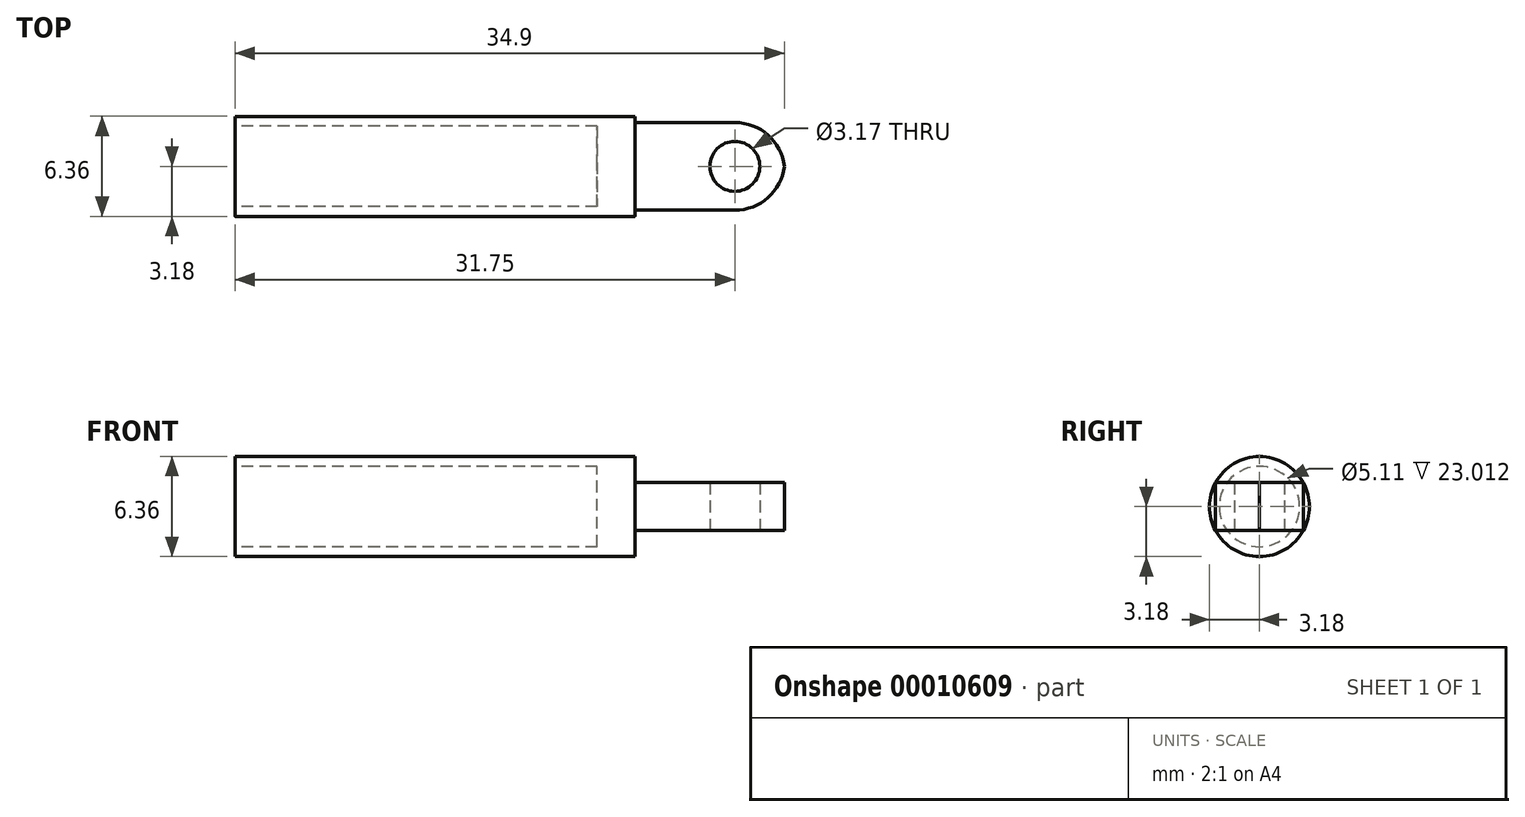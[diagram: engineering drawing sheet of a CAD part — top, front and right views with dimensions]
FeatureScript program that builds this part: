
annotation { "Feature Type Name" : "Feature", "Feature Type Description" : "" }
export const myFeature = defineFeature(function(context is Context, id is Id, definition is map)
    precondition{}
    {
        {
            var Q0;
            Q0=qCreatedBy(makeId("Right.planeOp"),FACE);
            var sketch = newSketch(context, id + "F0", { "sketchPlane" : qUnion([Q0])});
            skCircle(sketch, "E0", {"center": v(0, 0) * mm, "radius": 3.17 * mm});
            skCircle(sketch, "E1", {"center": v(0, 0) * mm, "radius": 2.55 * mm});
            skSolve(sketch);
        }
        {
            var Q0;
            Q0=qSketchRegion(id+"F0",true);
            var Q1;
            Q1=makeQuery(id+"F0.imprint","IMPRINT",FACE,{"disambiguationData":[TD([[makeQuery(id+"F0.imprint","IMPRINT",EDGE,{"derivedFrom":sQuery(id+"F0.wireOp",EDGE,"E1")}),1.0]])]});
            extrude(context, id + "F1", {"entities" : qUnion([Q0, Q1]), "depth" : 25.4 * mm});
        }
        {
            var Q0;
            Q0=makeQuery(id+"F0.imprint","IMPRINT",FACE,{"disambiguationData":[TD([[makeQuery(id+"F0.imprint","IMPRINT",EDGE,{"derivedFrom":sQuery(id+"F0.wireOp",EDGE,"E1")}),1.0]])]});
            extrude(context, id + "F2", {"entities" : qUnion([Q0]), "operationType" : NewBodyOperationType.REMOVE, "depth" : 23.01 * mm});
        }
        {
            var Q0;
            Q0=makeQuery(id+"F1.opExtrude","CAP_FACE",FACE,{"disambiguationData":[OSD([sQuery(id+"F0.wireOp",EDGE,"E0")])],"isStart":false});
            var sketch = newSketch(context, id + "F3", { "sketchPlane" : qUnion([Q0])});
            skCircle(sketch, "E2.0", {"center": v(0, 0) * mm, "radius": 3.17 * mm, "construction": true});
            skLineSegment(sketch, "E3.rect.bottom", {"start": v(-2.79, -1.52) * mm, "end": v(2.79, -1.52) * mm});
            skLineSegment(sketch, "E3.rect.top", {"start": v(-2.79, 1.52) * mm, "end": v(2.79, 1.52) * mm});
            skLineSegment(sketch, "E3.rect.left", {"start": v(-2.79, -1.52) * mm, "end": v(-2.79, 1.52) * mm});
            skLineSegment(sketch, "E3.rect.right", {"start": v(2.79, -1.52) * mm, "end": v(2.79, 1.52) * mm});
            skSolve(sketch);
        }
        {
            var Q0;
            Q0=qSketchRegion(id+"F3",true);
            extrude(context, id + "F4", {"entities" : qUnion([Q0]), "operationType" : NewBodyOperationType.ADD, "depth" : 9.52 * mm});
        }
        {
            var Q0;
            Q0=makeQuery(id+"F4.opExtrude","CAP_EDGE",EDGE,{"disambiguationData":[OSD([sQuery(id+"F3.wireOp",EDGE,"E3.rect.left")])],"isStart":false});
            var Q1;
            Q1=makeQuery(id+"F4.opExtrude","CAP_EDGE",EDGE,{"disambiguationData":[OSD([sQuery(id+"F3.wireOp",EDGE,"E3.rect.right")])],"isStart":false});
            fillet(context, id + "F5", {"entities" : qUnion([Q0, Q1]), "radius" : 3.17 * mm, "tangentPropagation" : true, "allowEdgeOverflow" : false});
        }
        {
            var Q0;
            Q0=makeQuery(id+"F4.opExtrude","SWEPT_FACE",FACE,{"disambiguationData":[OSD([sQuery(id+"F3.wireOp",EDGE,"E3.rect.bottom")])]});
            var sketch = newSketch(context, id + "F6", { "sketchPlane" : qUnion([Q0])});
            skLineSegment(sketch, "E4.0", {"start": v(25.4, 2.79) * mm, "end": v(25.4, -2.79) * mm, "construction": true});
            skLineSegment(sketch, "E5.0", {"start": v(31.75, -2.79) * mm, "end": v(25.4, -2.79) * mm, "construction": true});
            skLineSegment(sketch, "E6.0", {"start": v(31.75, 2.79) * mm, "end": v(25.4, 2.79) * mm, "construction": true});
            skLineSegment(sketch, "E7.0", {"start": v(0, 3.17) * mm, "end": v(0, -3.17) * mm, "construction": true});
            skCircle(sketch, "E8", {"center": v(31.75, 0) * mm, "radius": 1.59 * mm});
            skSolve(sketch);
        }
        {
            var Q0;
            Q0=qSketchRegion(id+"F6",true);
            extrude(context, id + "F7", {"entities" : qUnion([Q0]), "operationType" : NewBodyOperationType.REMOVE, "endBound" : BoundingType.THROUGH_ALL, "oppositeDirection" : true, "depth" : 25.4 * mm});
        }
    });
